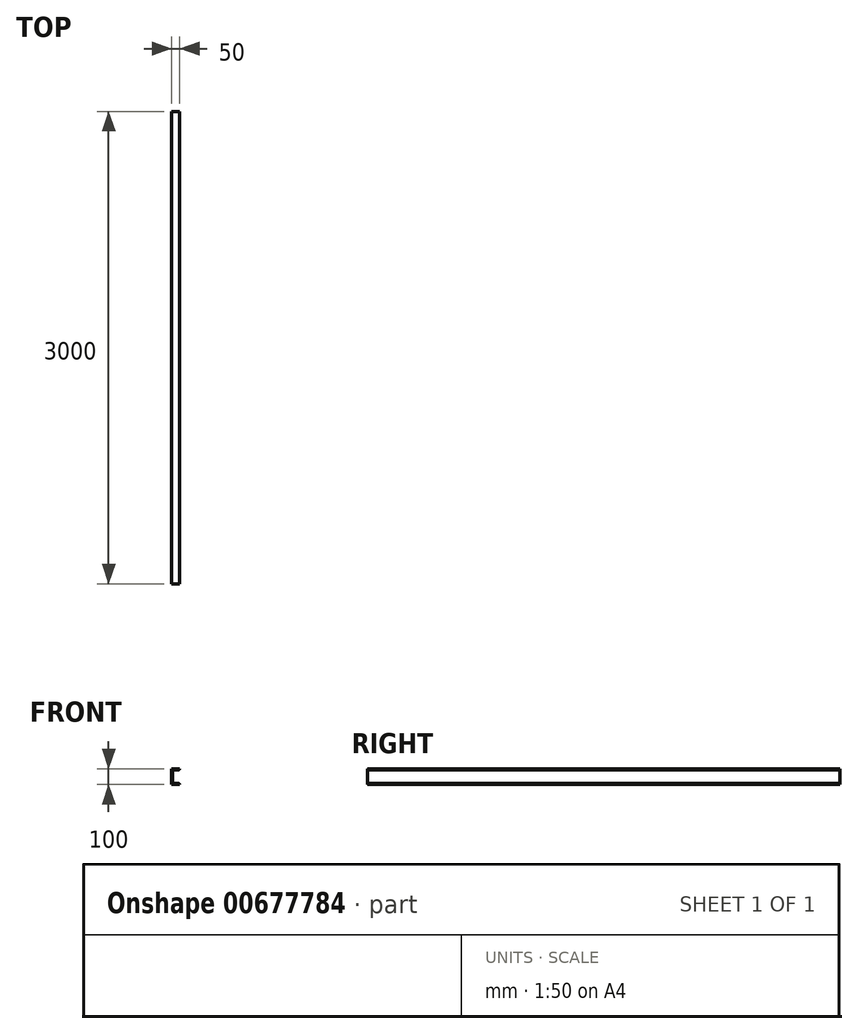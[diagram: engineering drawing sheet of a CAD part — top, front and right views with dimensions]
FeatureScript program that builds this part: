
annotation { "Feature Type Name" : "Feature", "Feature Type Description" : "" }
export const myFeature = defineFeature(function(context is Context, id is Id, definition is map)
    precondition{}
    {
        {
            var Q0;
            Q0=qCreatedBy(makeId("Front.planeOp"),FACE);
            var sketch = newSketch(context, id + "F0", { "sketchPlane" : qUnion([Q0])});
            skLineSegment(sketch, "E0.bottom", {"start": v(25, -50) * mm, "end": v(-25, -50) * mm});
            skLineSegment(sketch, "E0.top", {"start": v(25, 50) * mm, "end": v(-25, 50) * mm});
            skLineSegment(sketch, "E0.right", {"start": v(-25, -50) * mm, "end": v(-25, 50) * mm});
            skPoint(sketch, "E0.middle", {"position": v(0, 0) * mm});
            skLineSegment(sketch, "E1.0", {"start": v(20, -44) * mm, "end": v(-14, -44) * mm});
            skLineSegment(sketch, "E1.1", {"start": v(-19, -39) * mm, "end": v(-19, 39) * mm});
            skLineSegment(sketch, "E1.2", {"start": v(20, 44) * mm, "end": v(-14, 44) * mm});
            skLineSegment(sketch, "E2", {"start": v(25, 50) * mm, "end": v(25, 49) * mm});
            skLineSegment(sketch, "E3", {"start": v(25, -50) * mm, "end": v(25, -49) * mm});
            skPoint(sketch, "E4.visualSharp", {"position": v(25, -44) * mm});
            skArc(sketch, "E4.filletArc", {"start": v(25, -49) * mm, "mid": v(23.54, -45.46) * mm, "end": v(20, -44) * mm});
            skPoint(sketch, "E5.visualSharp", {"position": v(-19, -44) * mm});
            skArc(sketch, "E5.filletArc", {"start": v(-19, -39) * mm, "mid": v(-17.54, -42.54) * mm, "end": v(-14, -44) * mm});
            skPoint(sketch, "E6.visualSharp", {"position": v(-19, 44) * mm});
            skArc(sketch, "E6.filletArc", {"start": v(-14, 44) * mm, "mid": v(-17.54, 42.54) * mm, "end": v(-19, 39) * mm});
            skPoint(sketch, "E7.visualSharp", {"position": v(25, 44) * mm});
            skArc(sketch, "E7.filletArc", {"start": v(20, 44) * mm, "mid": v(23.54, 45.46) * mm, "end": v(25, 49) * mm});
            skSolve(sketch);
        }
        {
            var Q0;
            Q0 = qSketchRegion(id + "F0", true);
            extrude(context, id + "F1", {"entities" : qUnion([Q0]), "depth" : 3000 * mm, "offsetDistance" : 25 * mm});
        }
    });
